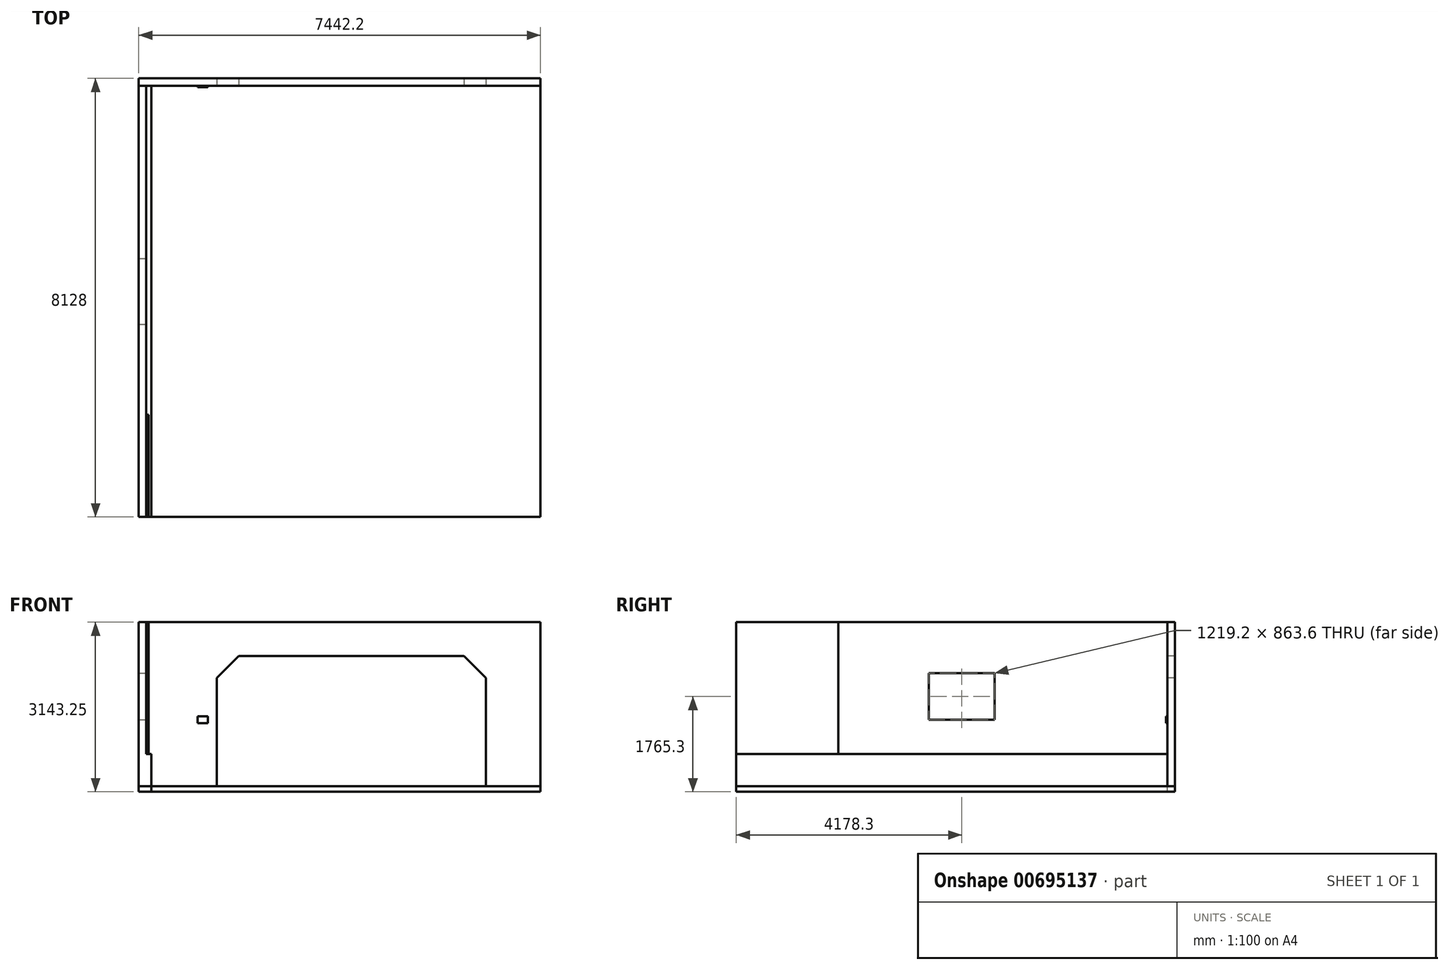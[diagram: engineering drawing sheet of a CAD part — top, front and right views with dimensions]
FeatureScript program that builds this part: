
annotation { "Feature Type Name" : "Feature", "Feature Type Description" : "" }
export const myFeature = defineFeature(function(context is Context, id is Id, definition is map)
    precondition{}
    {
        {
            var Q0;
            Q0=qCreatedBy(makeId("Right.planeOp"),FACE);
            var sketch = newSketch(context, id + "F0", { "sketchPlane" : qUnion([Q0])});
            skLineSegment(sketch, "E0.bottom", {"start": v(-3997.1, -1633.6) * mm, "end": v(3991.2, -1633.6) * mm});
            skLineSegment(sketch, "E0.top", {"start": v(-3997.1, 1408.05) * mm, "end": v(3991.2, 1408.05) * mm});
            skLineSegment(sketch, "E0.left", {"start": v(-3997.1, -1633.6) * mm, "end": v(-3997.1, 1408.05) * mm});
            skLineSegment(sketch, "E0.right", {"start": v(3991.2, -1633.6) * mm, "end": v(3991.2, 1408.05) * mm});
            skSolve(sketch);
        }
        {
            var Q0;
            Q0=makeQuery(id+"F0.imprint","IMPRINT",FACE,{"disambiguationData":[TD([[makeQuery(id+"F0.imprint","IMPRINT",EDGE,{"derivedFrom":sQuery(id+"F0.wireOp",EDGE,"E0.bottom")}),1.0]])]});
            extrude(context, id + "F1", {"entities" : qUnion([Q0]), "depth" : 139.7 * mm, "offsetDistance" : 25.4 * mm});
        }
        {
            var Q0;
            Q0=makeQuery(id+"F1.opExtrude","CAP_FACE",FACE,{"disambiguationData":[OSD([sQuery(id+"F0.wireOp",EDGE,"E0.bottom"),sQuery(id+"F0.wireOp",EDGE,"E0.top"),sQuery(id+"F0.wireOp",EDGE,"E0.left"),sQuery(id+"F0.wireOp",EDGE,"E0.right")])],"isStart":false});
            var sketch = newSketch(context, id + "F2", { "sketchPlane" : qUnion([Q0])});
            skLineSegment(sketch, "E1.bottom", {"start": v(-428.4, 461.9) * mm, "end": v(790.8, 461.9) * mm});
            skLineSegment(sketch, "E1.top", {"start": v(-428.4, -401.7) * mm, "end": v(790.8, -401.7) * mm});
            skLineSegment(sketch, "E1.left", {"start": v(-428.4, 461.9) * mm, "end": v(-428.4, -401.7) * mm});
            skLineSegment(sketch, "E1.right", {"start": v(790.8, 461.9) * mm, "end": v(790.8, -401.7) * mm});
            skSolve(sketch);
        }
        {
            var Q0;
            Q0=makeQuery(id+"F2.imprint","IMPRINT",FACE,{"disambiguationData":[TD([[makeQuery(id+"F2.imprint","IMPRINT",EDGE,{"derivedFrom":sQuery(id+"F2.wireOp",EDGE,"E1.bottom")}),-1.0]])]});
            var Q1;
            Q1=makeQuery(id+"F1.opExtrude","CAP_FACE",FACE,{"disambiguationData":[OSD([sQuery(id+"F0.wireOp",EDGE,"E0.bottom"),sQuery(id+"F0.wireOp",EDGE,"E0.top"),sQuery(id+"F0.wireOp",EDGE,"E0.left"),sQuery(id+"F0.wireOp",EDGE,"E0.right")])],"isStart":true});
            extrude(context, id + "F3", {"entities" : qUnion([Q0]), "operationType" : NewBodyOperationType.REMOVE, "endBound" : BoundingType.UP_TO_NEXT, "oppositeDirection" : true, "depth" : 25.4 * mm, "endBoundEntityFace" : qUnion([Q1]), "offsetDistance" : 25.4 * mm});
        }
        {
            var Q0;
            Q0=makeQuery(id+"F1.opExtrude","SWEPT_FACE",FACE,{"disambiguationData":[OSD([sQuery(id+"F0.wireOp",EDGE,"E0.left")])]});
            var sketch = newSketch(context, id + "F4", { "sketchPlane" : qUnion([Q0])});
            skLineSegment(sketch, "E2.bottom", {"start": v(139.7, -1633.6) * mm, "end": v(234.95, -1633.6) * mm});
            skLineSegment(sketch, "E2.top", {"start": v(139.7, -1036.7) * mm, "end": v(234.95, -1036.7) * mm});
            skLineSegment(sketch, "E2.left", {"start": v(139.7, -1633.6) * mm, "end": v(139.7, -1036.7) * mm});
            skLineSegment(sketch, "E2.right", {"start": v(234.95, -1633.6) * mm, "end": v(234.95, -1036.7) * mm});
            skSolve(sketch);
        }
        {
            var Q0;
            Q0=makeQuery(id+"F4.imprint","IMPRINT",FACE,{"disambiguationData":[TD([[makeQuery(id+"F4.imprint","IMPRINT",EDGE,{"derivedFrom":sQuery(id+"F4.wireOp",EDGE,"E2.bottom")}),1.0]])]});
            var Q1;
            Q1=makeQuery(id+"F1.opExtrude","SWEPT_FACE",FACE,{"disambiguationData":[OSD([sQuery(id+"F0.wireOp",EDGE,"E0.right")])]});
            extrude(context, id + "F5", {"entities" : qUnion([Q0]), "operationType" : NewBodyOperationType.ADD, "endBound" : BoundingType.UP_TO_SURFACE, "oppositeDirection" : true, "depth" : 25.4 * mm, "endBoundEntityFace" : qUnion([Q1]), "offsetDistance" : 25.4 * mm});
        }
        {
            var Q0;
            Q0=makeQuery(id+"F1.opExtrude","CAP_FACE",FACE,{"disambiguationData":[OSD([sQuery(id+"F0.wireOp",EDGE,"E0.bottom"),sQuery(id+"F0.wireOp",EDGE,"E0.top"),sQuery(id+"F0.wireOp",EDGE,"E0.left"),sQuery(id+"F0.wireOp",EDGE,"E0.right")])],"isStart":true});
            var sketch = newSketch(context, id + "F6", { "sketchPlane" : qUnion([Q0])});
            skLineSegment(sketch, "E3.bottom", {"start": v(-3991.2, 1408.05) * mm, "end": v(-4130.9, 1408.05) * mm});
            skLineSegment(sketch, "E3.top", {"start": v(-3991.2, -1633.6) * mm, "end": v(-4130.9, -1633.6) * mm});
            skLineSegment(sketch, "E3.left", {"start": v(-3991.2, 1408.05) * mm, "end": v(-3991.2, -1633.6) * mm});
            skLineSegment(sketch, "E3.right", {"start": v(-4130.9, 1408.05) * mm, "end": v(-4130.9, -1633.6) * mm});
            skSolve(sketch);
        }
        {
            var Q0;
            Q0=makeQuery(id+"F6.imprint","IMPRINT",FACE,{"disambiguationData":[TD([[makeQuery(id+"F6.imprint","IMPRINT",EDGE,{"derivedFrom":sQuery(id+"F6.wireOp",EDGE,"E3.bottom")}),1.0]])]});
            extrude(context, id + "F7", {"entities" : qUnion([Q0]), "oppositeDirection" : true, "depth" : 7442.2 * mm, "offsetDistance" : 25.4 * mm});
        }
        {
            var Q0;
            Q0=makeQuery(id+"F7.opExtrude","SWEPT_FACE",FACE,{"disambiguationData":[OSD([sQuery(id+"F6.wireOp",EDGE,"E3.left")])]});
            var sketch = newSketch(context, id + "F8", { "sketchPlane" : qUnion([Q0])});
            skLineSegment(sketch, "E4.bottom", {"start": v(1447.8, -1633.6) * mm, "end": v(6429.1, -1633.6) * mm});
            skLineSegment(sketch, "E4.top", {"start": v(1854.2, 779.4) * mm, "end": v(6022.7, 779.4) * mm});
            skLineSegment(sketch, "E4.left", {"start": v(1447.8, -1633.6) * mm, "end": v(1447.8, 373) * mm});
            skLineSegment(sketch, "E4.right", {"start": v(6429.1, -1633.6) * mm, "end": v(6429.1, 373) * mm});
            skLineSegment(sketch, "E5", {"start": v(1447.8, 373) * mm, "end": v(1854.2, 779.4) * mm});
            skLineSegment(sketch, "E6", {"start": v(6022.7, 779.4) * mm, "end": v(6429.1, 373) * mm});
            skSolve(sketch);
        }
        {
            var Q0;
            Q0=makeQuery(id+"F8.imprint","IMPRINT",FACE,{"disambiguationData":[TD([[makeQuery(id+"F8.imprint","IMPRINT",EDGE,{"derivedFrom":sQuery(id+"F8.wireOp",EDGE,"E4.bottom")}),-1.0]])]});
            extrude(context, id + "F9", {"entities" : qUnion([Q0]), "operationType" : NewBodyOperationType.REMOVE, "endBound" : BoundingType.UP_TO_NEXT, "oppositeDirection" : true, "depth" : 25.4 * mm, "offsetDistance" : 25.4 * mm});
        }
        {
            var Q0;
            Q0=makeQuery(id+"F5.boolean.opBoolean","MERGE",FACE,{"derivedFrom":[makeQuery(id+"F1.opExtrude","SWEPT_FACE",FACE,{"disambiguationData":[OSD([sQuery(id+"F0.wireOp",EDGE,"E0.bottom")])]}),makeQuery(id+"F5.opExtrude","SWEPT_FACE",FACE,{"disambiguationData":[OSD([sQuery(id+"F4.wireOp",EDGE,"E2.bottom")])]})]});
            var sketch = newSketch(context, id + "F10", { "sketchPlane" : qUnion([Q0])});
            skLineSegment(sketch, "E7.bottom", {"start": v(0, 3997.1) * mm, "end": v(7442.2, 3997.1) * mm});
            skLineSegment(sketch, "E7.top", {"start": v(0, -4130.9) * mm, "end": v(7442.2, -4130.9) * mm});
            skLineSegment(sketch, "E7.left", {"start": v(0, 3997.1) * mm, "end": v(0, -4130.9) * mm});
            skLineSegment(sketch, "E7.right", {"start": v(7442.2, 3997.1) * mm, "end": v(7442.2, -4130.9) * mm});
            skSolve(sketch);
        }
        {
            var Q0;
            {var subQ4=sQuery(id+"F10.wireOp",EDGE,"E7.top");Q0=makeQuery(id+"F10.imprint","IMPRINT",FACE,{"disambiguationData":[TD([[makeQuery(id+"F10.imprint","IMPRINT",EDGE,{"derivedFrom":subQ4}),1.0]])]});}
            extrude(context, id + "F11", {"entities" : qUnion([Q0]), "depth" : 101.6 * mm, "offsetDistance" : 25.4 * mm});
        }
        {
            var Q0;
            Q0=makeQuery(id+"F5.boolean.opBoolean","MERGE",FACE,{"derivedFrom":[makeQuery(id+"F1.opExtrude","SWEPT_FACE",FACE,{"disambiguationData":[OSD([sQuery(id+"F0.wireOp",EDGE,"E0.left")])]}),makeQuery(id+"F5.opExtrude","CAP_FACE",FACE,{"disambiguationData":[OSD([sQuery(id+"F4.wireOp",EDGE,"E2.bottom"),sQuery(id+"F4.wireOp",EDGE,"E2.top"),sQuery(id+"F4.wireOp",EDGE,"E2.left"),sQuery(id+"F4.wireOp",EDGE,"E2.right")])],"isStart":true})]});
            var sketch = newSketch(context, id + "F12", { "sketchPlane" : qUnion([Q0])});
            skLineSegment(sketch, "E8.bottom", {"start": v(139.7, 1408.05) * mm, "end": v(184.15, 1408.05) * mm});
            skLineSegment(sketch, "E8.top", {"start": v(139.7, -1036.7) * mm, "end": v(234.95, -1036.7) * mm});
            skLineSegment(sketch, "E8.left", {"start": v(139.7, 1408.05) * mm, "end": v(139.7, -1036.7) * mm});
            skLineSegment(sketch, "E8.right", {"start": v(184.15, 1408.05) * mm, "end": v(184.15, -1036.7) * mm});
            skSolve(sketch);
        }
        {
            var Q0;
            Q0=makeQuery(id+"F12.imprint","IMPRINT",FACE,{"disambiguationData":[TD([[makeQuery(id+"F12.imprint","IMPRINT",EDGE,{"derivedFrom":sQuery(id+"F12.wireOp",EDGE,"E8.bottom")}),-1.0]])]});
            extrude(context, id + "F13", {"entities" : qUnion([Q0]), "oppositeDirection" : true, "depth" : 1892.3 * mm, "offsetDistance" : 25.4 * mm});
        }
        {
            var Q0;
            Q0=makeQuery(id+"F7.opExtrude","SWEPT_FACE",FACE,{"disambiguationData":[OSD([sQuery(id+"F6.wireOp",EDGE,"E3.left")])]});
            var sketch = newSketch(context, id + "F14", { "sketchPlane" : qUnion([Q0])});
            skLineSegment(sketch, "E9.bottom", {"start": v(1092.2, -465.2) * mm, "end": v(1282.7, -465.2) * mm});
            skLineSegment(sketch, "E9.top", {"start": v(1092.2, -338.2) * mm, "end": v(1282.7, -338.2) * mm});
            skLineSegment(sketch, "E9.left", {"start": v(1092.2, -338.2) * mm, "end": v(1092.2, -465.2) * mm});
            skLineSegment(sketch, "E9.right", {"start": v(1282.7, -338.2) * mm, "end": v(1282.7, -465.2) * mm});
            skSolve(sketch);
        }
        {
            var Q0;
            Q0=makeQuery(id+"F14.imprint","IMPRINT",FACE,{"disambiguationData":[TD([[makeQuery(id+"F14.imprint","IMPRINT",EDGE,{"derivedFrom":sQuery(id+"F14.wireOp",EDGE,"E9.bottom")}),1.0]])]});
            extrude(context, id + "F15", {"entities" : qUnion([Q0]), "depth" : 25.4 * mm, "offsetDistance" : 25.4 * mm});
        }
    });
